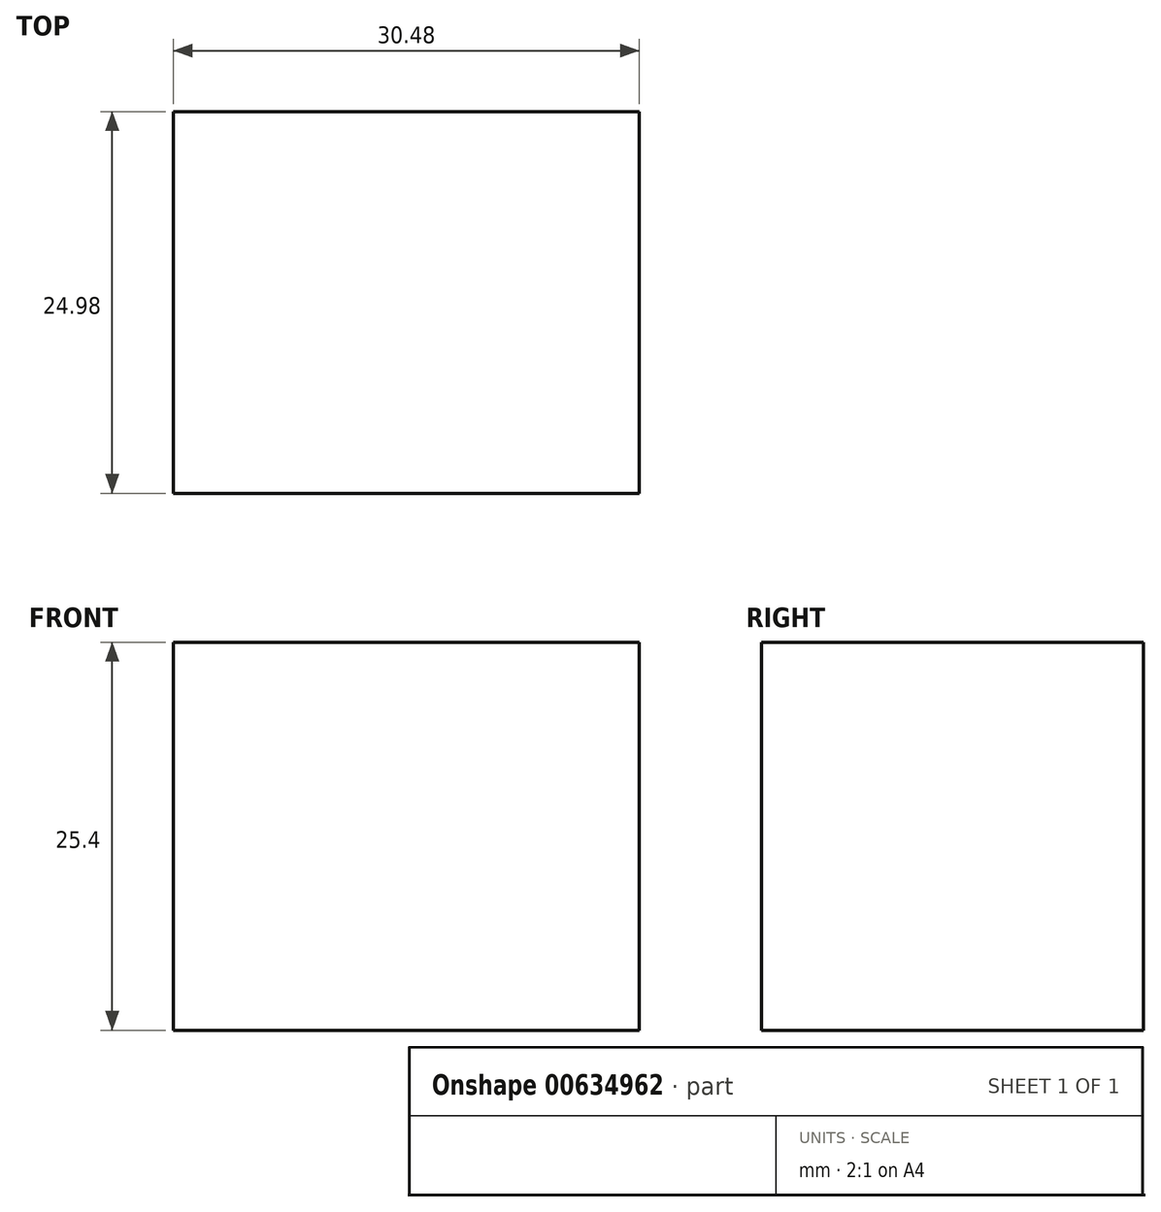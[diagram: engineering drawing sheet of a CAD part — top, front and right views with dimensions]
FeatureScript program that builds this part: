
annotation { "Feature Type Name" : "Feature", "Feature Type Description" : "" }
export const myFeature = defineFeature(function(context is Context, id is Id, definition is map)
    precondition{}
    {
        {
            var Q0;
            Q0=qCreatedBy(makeId("Top.planeOp"),FACE);
            var sketch = newSketch(context, id + "F0", { "sketchPlane" : qUnion([Q0])});
            skLineSegment(sketch, "E0.bottom", {"start": v(15.24, 12.49) * mm, "end": v(-15.24, 12.49) * mm});
            skLineSegment(sketch, "E0.top", {"start": v(15.24, -12.49) * mm, "end": v(-15.24, -12.49) * mm});
            skLineSegment(sketch, "E0.left", {"start": v(15.24, 12.49) * mm, "end": v(15.24, -12.49) * mm});
            skLineSegment(sketch, "E0.right", {"start": v(-15.24, 12.49) * mm, "end": v(-15.24, -12.49) * mm});
            skPoint(sketch, "E0.middle", {"position": v(0, 0) * mm});
            skSolve(sketch);
        }
        {
            var Q0;
            Q0=qCreatedBy(makeId("Top.planeOp"),FACE);
            var sketch = newSketch(context, id + "F1", { "sketchPlane" : qUnion([Q0])});
            skLineSegment(sketch, "E1", {"start": v(15.25, -4.06) * mm, "end": v(39.87, -4.06) * mm});
            skLineSegment(sketch, "E2", {"start": v(39.87, -4.06) * mm, "end": v(23.08, -28.67) * mm});
            skLineSegment(sketch, "E3", {"start": v(23.08, -28.67) * mm, "end": v(15.25, -12.73) * mm});
            skSolve(sketch);
        }
        {
            var Q0;
            Q0 = qSketchRegion(id + "F1", true);
            var Q1;
            Q1=makeQuery(id+"F0.imprint","IMPRINT",FACE,{"disambiguationData":[TD([[makeQuery(id+"F0.imprint","IMPRINT",EDGE,{"derivedFrom":sQuery(id+"F0.wireOp",EDGE,"E0.bottom")}),1.0]])]});
            extrude(context, id + "F2", {"entities" : qUnion([Q0, Q1]), "depth" : 25.4 * mm, "offsetDistance" : 25.4 * mm});
        }
    });
